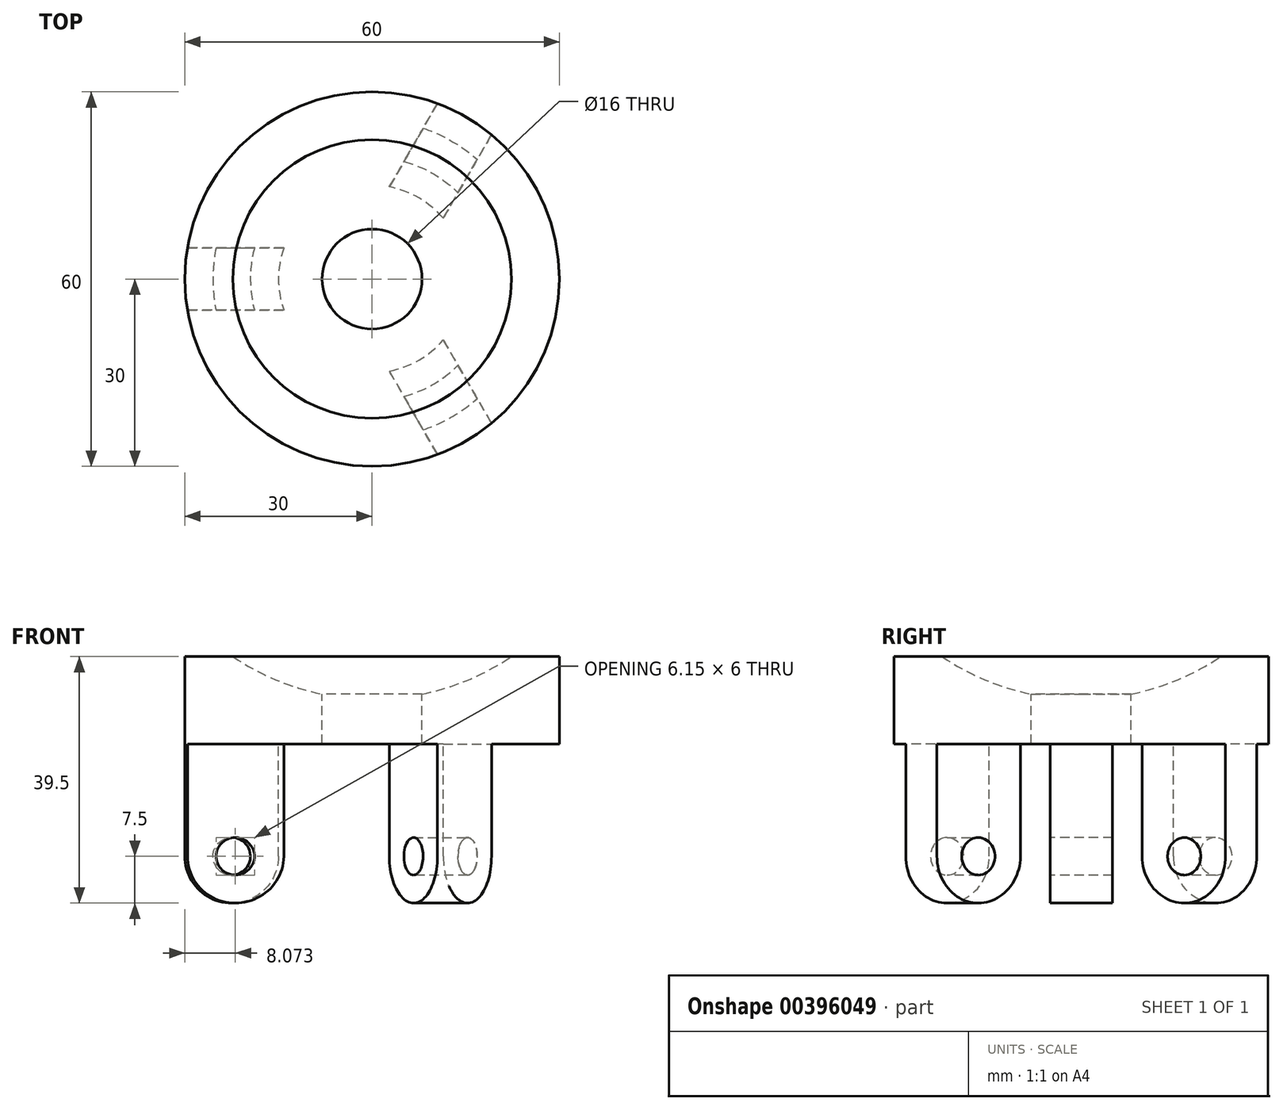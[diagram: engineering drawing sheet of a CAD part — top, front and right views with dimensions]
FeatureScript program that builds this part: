
annotation { "Feature Type Name" : "Feature", "Feature Type Description" : "" }
export const myFeature = defineFeature(function(context is Context, id is Id, definition is map)
    precondition{}
    {
        {
            var Q0;
            Q0=qCreatedBy(makeId("Front.planeOp"),FACE);
            var sketch = newSketch(context, id + "F0", { "sketchPlane" : qUnion([Q0])});
            skLineSegment(sketch, "E0", {"start": v(-22.32, 0) * mm, "end": v(-30, 0) * mm});
            skLineSegment(sketch, "E1", {"start": v(-30, 0) * mm, "end": v(-30, -32) * mm});
            skArc(sketch, "E2", {"start": v(-30, -32) * mm, "mid": v(-22.5, -39.5) * mm, "end": v(-15, -32) * mm});
            skLineSegment(sketch, "E3", {"start": v(-15, -32) * mm, "end": v(-15, -14) * mm});
            skLineSegment(sketch, "E4", {"start": v(-15, -14) * mm, "end": v(-8, -14) * mm});
            skLineSegment(sketch, "E5", {"start": v(-8, -14) * mm, "end": v(-8, -6) * mm});
            skArc(sketch, "E6", {"start": v(-22.32, 0) * mm, "mid": v(-15.46, -3.7) * mm, "end": v(-8, -6) * mm});
            skCircle(sketch, "E7", {"center": v(-22.5, -32) * mm, "radius": 3 * mm});
            skLineSegment(sketch, "E8", {"start": v(0, 0) * mm, "end": v(0, -14) * mm});
            skSolve(sketch);
        }
        {
            var Q0;
            Q0=qCreatedBy(makeId("Top.planeOp"),FACE);
            var sketch = newSketch(context, id + "F1", { "sketchPlane" : qUnion([Q0])});
            skCircle(sketch, "E9", {"center": v(0, 0) * mm, "radius": 30 * mm});
            skCircle(sketch, "E10", {"center": v(0, 0) * mm, "radius": 8 * mm});
            skLineSegment(sketch, "E11", {"start": v(-30, 0) * mm, "end": v(0, 0) * mm});
            skLineSegment(sketch, "E12", {"start": v(15, 25.98) * mm, "end": v(0, 0) * mm});
            skLineSegment(sketch, "E13", {"start": v(0, 0) * mm, "end": v(15, -25.98) * mm});
            skSolve(sketch);
        }
        {
            var Q0;
            Q0=makeQuery(id+"F0.imprint","IMPRINT",FACE,{"disambiguationData":[TD([[makeQuery(id+"F0.imprint","IMPRINT",EDGE,{"derivedFrom":sQuery(id+"F0.wireOp",EDGE,"E0")}),1.0]])]});
            var Q1;
            Q1=sQuery(id+"F0.wireOp",EDGE,"E8");
            revolve(context, id + "F2", {"entities" : qUnion([Q0]), "axis" : qUnion([Q1]), "revolveType" : RevolveType.FULL});
        }
        {
            var Q0;
            Q0=qCreatedBy(makeId("Top.planeOp"),FACE);
            cPlane(context, id + "F3", {"entities" : qUnion([Q0]), "cplaneType" : CPlaneType.OFFSET, "offset" : (32 - 18) * mm, "oppositeDirection" : true, "width" : 150 * mm, "height" : 150 * mm});
        }
        {
            var Q0;
            Q0=qCreatedBy(id+"F3.planeOp",FACE);
            var sketch = newSketch(context, id + "F4", { "sketchPlane" : qUnion([Q0])});
            skCircle(sketch, "E14", {"center": v(0, 0) * mm, "radius": 30 * mm});
            skLineSegment(sketch, "E15", {"start": v(-29.58, -5) * mm, "end": v(-2.89, -5) * mm});
            skLineSegment(sketch, "E16", {"start": v(-2.89, -5) * mm, "end": v(10.46, -28.12) * mm});
            skLineSegment(sketch, "E17", {"start": v(10.46, -28.12) * mm, "end": v(19.12, -23.12) * mm});
            skLineSegment(sketch, "E18", {"start": v(19.12, -23.12) * mm, "end": v(5.77, 0) * mm});
            skLineSegment(sketch, "E19", {"start": v(5.77, 0) * mm, "end": v(19.12, 23.12) * mm});
            skLineSegment(sketch, "E20", {"start": v(19.12, 23.12) * mm, "end": v(10.46, 28.12) * mm});
            skLineSegment(sketch, "E21", {"start": v(10.46, 28.12) * mm, "end": v(-2.89, 5) * mm});
            skLineSegment(sketch, "E22", {"start": v(-2.89, 5) * mm, "end": v(-29.58, 5) * mm});
            skLineSegment(sketch, "E23", {"start": v(-29.58, 5) * mm, "end": v(-29.58, -5) * mm});
            skSolve(sketch);
        }
        {
            var Q0;
            {var subQ0=sQuery(id+"F4.wireOp",EDGE,"E21");Q0=makeQuery(id+"F4.imprint","IMPRINT",FACE,{"disambiguationData":[TD([[makeQuery(id+"F4.imprint","IMPRINT",EDGE,{"derivedFrom":subQ0}),-1.0]])]});}
            var Q1;
            {var subQ0=sQuery(id+"F4.wireOp",EDGE,"E18");Q1=makeQuery(id+"F4.imprint","IMPRINT",FACE,{"disambiguationData":[TD([[makeQuery(id+"F4.imprint","IMPRINT",EDGE,{"derivedFrom":subQ0}),-1.0]])]});}
            var Q2;
            {var subQ0=sQuery(id+"F4.wireOp",EDGE,"E15");Q2=makeQuery(id+"F4.imprint","IMPRINT",FACE,{"disambiguationData":[TD([[makeQuery(id+"F4.imprint","IMPRINT",EDGE,{"derivedFrom":subQ0}),-1.0]])]});}
            extrude(context, id + "F5", {"entities" : qUnion([Q0, Q1, Q2]), "operationType" : NewBodyOperationType.REMOVE, "endBound" : BoundingType.THROUGH_ALL, "oppositeDirection" : true, "depth" : 28 * mm});
        }
    });
